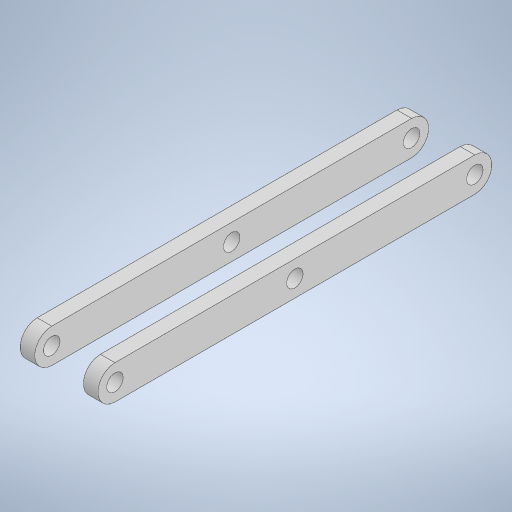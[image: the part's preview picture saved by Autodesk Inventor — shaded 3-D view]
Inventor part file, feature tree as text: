
AUTODESK INVENTOR PART (.ipt)
format: ipt  version: 2024.3 (Build 283343000, 343)  size: 257,024 bytes
history: native  units: mm
features: sketch x2, extrude x2, hole x1
ambient origin geometry x8: Origin, YZ Plane, XZ Plane, XY Plane, X Axis, Y Axis, Z Axis, Center Point
bodies: Body1 (feature_tree)
feature tree (5):
  sketch  "Sketch1"  dims[d14=7.0mm d15=81.0mm]
  extrude  "Extrusión3"  Depth=7.0mm
  extrude  "Extrusión4"  Depth=16.0mm TaperAngle=0.0deg
  hole  "Agujero1"  [1 undecoded]
  sketch  "Boceto2"  dims[d16=3.0mm d17=16.0mm d18=0.0mm d19=10.0mm d20=0.0mm d21=3.4mm d22=6.0mm d23=6.3mm d24=2.0mm d25=90.0deg d26=8.0mm d27=20.594885mm]
note: 1 required parameter value undecoded (feature->parameter linkage not recoverable at this tier; creation-order binding heuristic only, values carry confidence <= 0.55)
